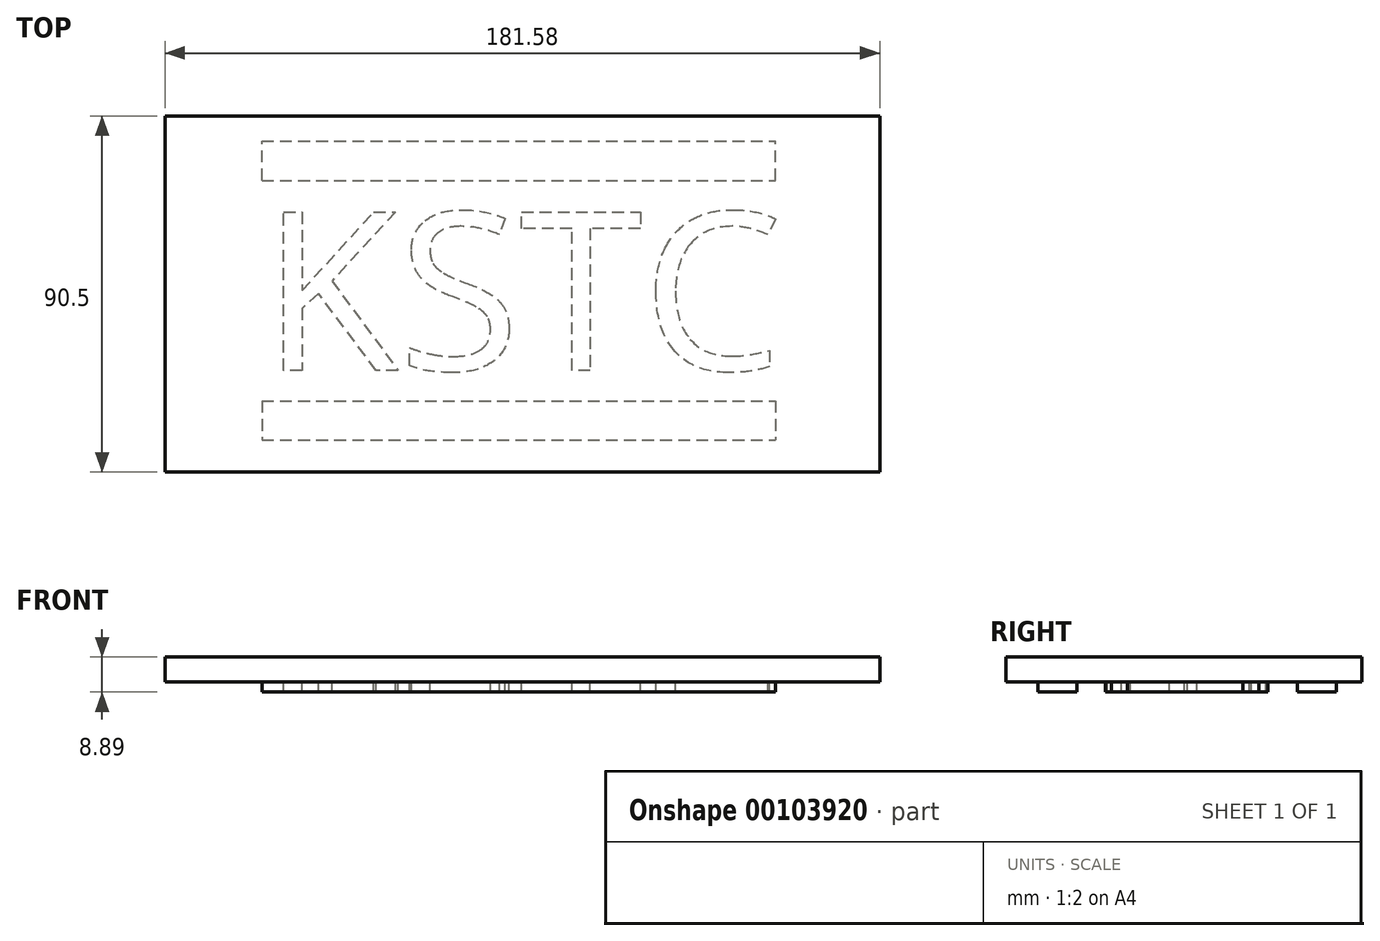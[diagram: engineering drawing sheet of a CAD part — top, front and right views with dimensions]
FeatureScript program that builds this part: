
annotation { "Feature Type Name" : "Feature", "Feature Type Description" : "" }
export const myFeature = defineFeature(function(context is Context, id is Id, definition is map)
    precondition{}
    {
        {
            var Q0;
            Q0=qCreatedBy(makeId("Top.planeOp"),FACE);
            var sketch = newSketch(context, id + "F0", { "sketchPlane" : qUnion([Q0])});
            skText(sketch, "E0", { "text": "KSTC", "fontName": "OpenSans-Regular.ttf"});
            skLineSegment(sketch, "E1.bottom", {"start": v(-66.2, 28.85) * mm, "end": v(64.35, 28.85) * mm});
            skLineSegment(sketch, "E1.top", {"start": v(-66.2, 38.8) * mm, "end": v(64.35, 38.8) * mm});
            skLineSegment(sketch, "E1.left", {"start": v(-66.2, 28.85) * mm, "end": v(-66.2, 38.8) * mm});
            skLineSegment(sketch, "E1.right", {"start": v(64.35, 28.85) * mm, "end": v(64.35, 38.8) * mm});
            skLineSegment(sketch, "E2.bottom", {"start": v(-66.2, -27.15) * mm, "end": v(64.35, -27.15) * mm});
            skLineSegment(sketch, "E2.top", {"start": v(-66.2, -37.1) * mm, "end": v(64.35, -37.1) * mm});
            skLineSegment(sketch, "E2.left", {"start": v(-66.2, -27.15) * mm, "end": v(-66.2, -37.1) * mm});
            skLineSegment(sketch, "E2.right", {"start": v(64.35, -27.15) * mm, "end": v(64.35, -37.1) * mm});
            const initialGuessF0  = {"E0": [-0.0662, -0.01942, 1, 0, 0.04057]};
            skSetInitialGuess(sketch, initialGuessF0);
            skSolve(sketch);
        }
        {
            var Q0;
            Q0=qCreatedBy(makeId("Top.planeOp"),FACE);
            var sketch = newSketch(context, id + "F1", { "sketchPlane" : qUnion([Q0])});
            skLineSegment(sketch, "E3.bottom", {"start": v(-90.79, -45.25) * mm, "end": v(90.79, -45.25) * mm});
            skLineSegment(sketch, "E3.top", {"start": v(-90.79, 45.25) * mm, "end": v(90.79, 45.25) * mm});
            skLineSegment(sketch, "E3.left", {"start": v(-90.79, -45.25) * mm, "end": v(-90.79, 45.25) * mm});
            skLineSegment(sketch, "E3.right", {"start": v(90.79, -45.25) * mm, "end": v(90.79, 45.25) * mm});
            skPoint(sketch, "E3.middle", {"position": v(0, 0) * mm});
            skSolve(sketch);
        }
        {
            var Q0;
            Q0=makeQuery(id+"F1.imprint","IMPRINT",FACE,{"disambiguationData":[TD([[makeQuery(id+"F1.imprint","IMPRINT",EDGE,{"derivedFrom":sQuery(id+"F1.wireOp",EDGE,"E3.bottom")}),1.0]])]});
            extrude(context, id + "F2", {"entities" : qUnion([Q0]), "depth" : 6.35 * mm});
        }
        {
            var Q0;
            Q0 = qSketchRegion(id + "F0", true);
            extrude(context, id + "F3", {"entities" : qUnion([Q0]), "operationType" : NewBodyOperationType.ADD, "oppositeDirection" : true, "depth" : 2.54 * mm});
        }
    });
